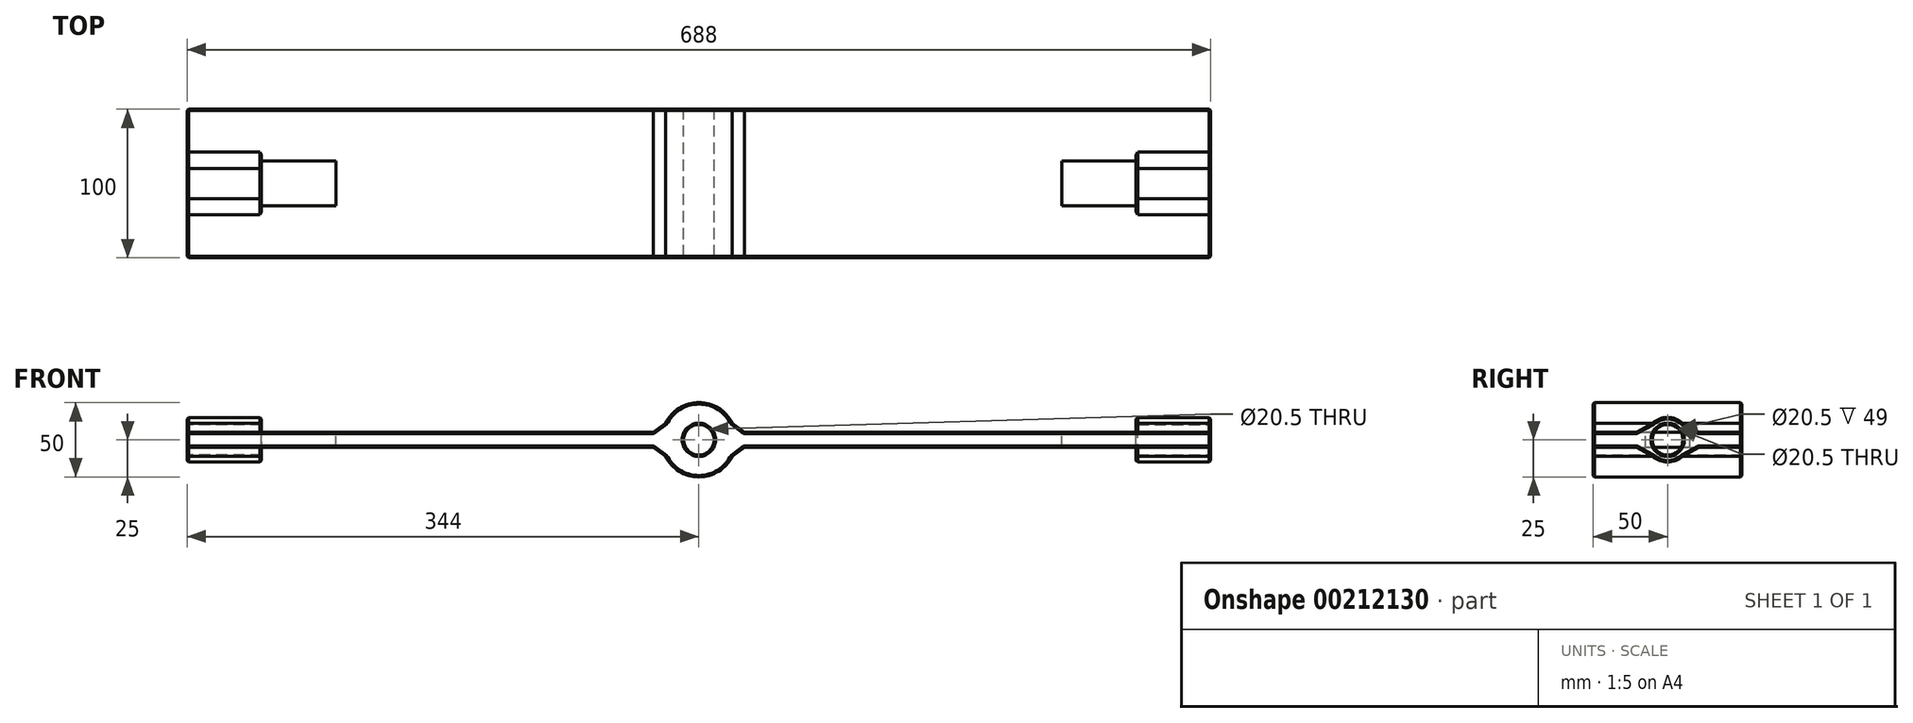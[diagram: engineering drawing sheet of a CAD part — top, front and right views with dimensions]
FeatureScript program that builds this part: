
annotation { "Feature Type Name" : "Feature", "Feature Type Description" : "" }
export const myFeature = defineFeature(function(context is Context, id is Id, definition is map)
    precondition{}
    {
        {
            var Q0;
            Q0=qCreatedBy(makeId("Top.planeOp"),FACE);
            var sketch = newSketch(context, id + "F0", { "sketchPlane" : qUnion([Q0])});
            skLineSegment(sketch, "E0.bottom", {"start": v(344.43, -50.2) * mm, "end": v(-339.43, -50.2) * mm});
            skLineSegment(sketch, "E0.top", {"start": v(344.43, 50.2) * mm, "end": v(-339.43, 50.2) * mm});
            skLineSegment(sketch, "E0.left", {"start": v(344.43, -50.2) * mm, "end": v(344.43, 50.2) * mm});
            skPoint(sketch, "E0.middle", {"position": v(0, 0) * mm});
            skLineSegment(sketch, "E1", {"start": v(-344.43, 14.8) * mm, "end": v(-244.43, 14.8) * mm});
            skLineSegment(sketch, "E2", {"start": v(-244.43, 14.8) * mm, "end": v(-244.43, -15.2) * mm});
            skLineSegment(sketch, "E3", {"start": v(-244.43, -15.2) * mm, "end": v(-344.43, -15.2) * mm});
            skLineSegment(sketch, "E4", {"start": v(-344.43, 45.2) * mm, "end": v(-344.43, 14.8) * mm});
            skLineSegment(sketch, "E5", {"start": v(-344.43, -15.2) * mm, "end": v(-344.43, -45.2) * mm});
            skPoint(sketch, "E6.visualSharp", {"position": v(-344.43, 50.2) * mm});
            skArc(sketch, "E6.filletArc", {"start": v(-339.43, 50.2) * mm, "mid": v(-342.97, 48.73) * mm, "end": v(-344.43, 45.2) * mm});
            skPoint(sketch, "E7.visualSharp", {"position": v(-344.43, -50.2) * mm});
            skArc(sketch, "E7.filletArc", {"start": v(-344.43, -45.2) * mm, "mid": v(-342.97, -48.73) * mm, "end": v(-339.43, -50.2) * mm});
            skLineSegment(sketch, "E8.MirrorCS", {"start": v(244.43, 14.8) * mm, "end": v(244.43, -15.2) * mm});
            skLineSegment(sketch, "E9.MirrorCS", {"start": v(344.43, 14.8) * mm, "end": v(244.43, 14.8) * mm});
            skLineSegment(sketch, "E10.MirrorCS", {"start": v(244.43, -15.2) * mm, "end": v(344.43, -15.2) * mm});
            skLineSegment(sketch, "E11.MirrorCS", {"start": v(344.43, -15.2) * mm, "end": v(344.43, -45.2) * mm});
            skArc(sketch, "E12.MirrorCS", {"start": v(344.43, -45.2) * mm, "mid": v(342.97, -48.73) * mm, "end": v(339.43, -50.2) * mm});
            skArc(sketch, "E13.MirrorCS", {"start": v(339.43, 50.2) * mm, "mid": v(342.97, 48.73) * mm, "end": v(344.43, 45.2) * mm});
            skLineSegment(sketch, "E14", {"start": v(0, 0) * mm, "end": v(0, 50.2) * mm, "construction": true});
            skLineSegment(sketch, "E15", {"start": v(0, 0) * mm, "end": v(0, -50.2) * mm, "construction": true});
            skLineSegment(sketch, "E16.0", {"start": v(27.5, 0) * mm, "end": v(27.5, 50.2) * mm});
            skLineSegment(sketch, "E17.0", {"start": v(-27.5, 0) * mm, "end": v(-27.5, -50.2) * mm});
            skLineSegment(sketch, "E18.0", {"start": v(27.5, 0) * mm, "end": v(27.5, -50.2) * mm});
            skLineSegment(sketch, "E19.0", {"start": v(-27.5, 0) * mm, "end": v(-27.5, 50.2) * mm});
            skSolve(sketch);
        }
        {
            var Q0;
            Q0=qCreatedBy(makeId("Front.planeOp"),FACE);
            var sketch = newSketch(context, id + "F1", { "sketchPlane" : qUnion([Q0])});
            skArc(sketch, "E20", {"start": v(-22.45, -11) * mm, "mid": v(0, -25) * mm, "end": v(22.45, -11) * mm});
            skCircle(sketch, "E21", {"center": v(0, 0) * mm, "radius": 10.25 * mm});
            skLineSegment(sketch, "E22", {"start": v(0, -11) * mm, "end": v(35.57, -11) * mm, "construction": true});
            skLineSegment(sketch, "E23.MirrorCS", {"start": v(0, -11) * mm, "end": v(-35.57, -11) * mm, "construction": true});
            skLineSegment(sketch, "E24.MirrorCS", {"start": v(0, 11) * mm, "end": v(35.57, 11) * mm, "construction": true});
            skLineSegment(sketch, "E25.MirrorCS", {"start": v(0, 11) * mm, "end": v(-35.57, 11) * mm, "construction": true});
            skLineSegment(sketch, "E26", {"start": v(-25, 0) * mm, "end": v(25, 0) * mm, "construction": true});
            skLineSegment(sketch, "E27.0", {"start": v(-24.5, -5) * mm, "end": v(24.5, -5) * mm, "construction": true});
            skLineSegment(sketch, "E28.0", {"start": v(-24.5, 5) * mm, "end": v(24.5, 5) * mm, "construction": true});
            skLineSegment(sketch, "E29", {"start": v(30.5, -14.84) * mm, "end": v(30.5, 11) * mm, "construction": true});
            skLineSegment(sketch, "E30", {"start": v(22.45, 11) * mm, "end": v(30.5, 5) * mm});
            skLineSegment(sketch, "E31", {"start": v(30.5, -5) * mm, "end": v(22.45, -11) * mm});
            skLineSegment(sketch, "E32", {"start": v(-24.5, -5) * mm, "end": v(-24.5, -5) * mm});
            skLineSegment(sketch, "E33", {"start": v(-24.5, 5) * mm, "end": v(-24.5, 5) * mm});
            skLineSegment(sketch, "E34", {"start": v(30.5, 5) * mm, "end": v(344, 5) * mm});
            skLineSegment(sketch, "E35", {"start": v(30.5, -5) * mm, "end": v(344, -5) * mm});
            skLineSegment(sketch, "E36", {"start": v(344, -5) * mm, "end": v(344, 5) * mm});
            skLineSegment(sketch, "E37", {"start": v(-30.5, 5) * mm, "end": v(-344, 5) * mm});
            skLineSegment(sketch, "E38", {"start": v(-30.5, -5) * mm, "end": v(-344, -5) * mm});
            skLineSegment(sketch, "E39", {"start": v(-344, 5) * mm, "end": v(-344, -5) * mm});
            skLineSegment(sketch, "E40", {"start": v(-30.5, 11) * mm, "end": v(-30.5, -11) * mm, "construction": true});
            skLineSegment(sketch, "E41", {"start": v(-22.45, 11) * mm, "end": v(-30.5, 5) * mm});
            skLineSegment(sketch, "E42", {"start": v(-30.5, -5) * mm, "end": v(-22.45, -11) * mm});
            skArc(sketch, "E43.trimOffspring", {"start": v(22.45, 11) * mm, "mid": v(0, 25) * mm, "end": v(-22.45, 11) * mm});
            skLineSegment(sketch, "E44.trimOffspring", {"start": v(30.5, -5) * mm, "end": v(33.37, -5) * mm, "construction": true});
            skSolve(sketch);
        }
        {
            var Q0;
            Q0=makeQuery(id+"F1.imprint","IMPRINT",FACE,{"disambiguationData":[TD([[makeQuery(id+"F1.imprint","IMPRINT",EDGE,{"derivedFrom":sQuery(id+"F1.wireOp",EDGE,"E20")}),1.0]])]});
            extrude(context, id + "F2", {"entities" : qUnion([Q0]), "depth" : 50 * mm, "hasSecondDirection" : true, "secondDirectionOppositeDirection" : true, "secondDirectionDepth" : 50 * mm});
        }
        {
            var Q0;
            Q0=qCreatedBy(makeId("Right.planeOp"),FACE);
            var sketch = newSketch(context, id + "F3", { "sketchPlane" : qUnion([Q0])});
            skCircle(sketch, "E45", {"center": v(0, 0) * mm, "radius": 10.25 * mm});
            skCircle(sketch, "E46", {"center": v(0, 0) * mm, "radius": 15 * mm});
            skSolve(sketch);
        }
        {
            var Q0;
            Q0=makeQuery(id+"F2.opExtrude","SWEPT_FACE",FACE,{"disambiguationData":[OSD([sQuery(id+"F1.wireOp",EDGE,"E39")])]});
            cPlane(context, id + "F4", {"entities" : qUnion([Q0]), "cplaneType" : CPlaneType.OFFSET, "offset" : 50 * mm, "oppositeDirection" : true, "width" : 150 * mm, "height" : 150 * mm});
        }
        {
            var Q0;
            Q0=makeQuery(id+"F2.opExtrude","SWEPT_FACE",FACE,{"disambiguationData":[OSD([sQuery(id+"F1.wireOp",EDGE,"E39")])]});
            var sketch = newSketch(context, id + "F5", { "sketchPlane" : qUnion([Q0])});
            skLineSegment(sketch, "E47.bottom", {"start": v(-15, 5) * mm, "end": v(-14.14, 5) * mm});
            skLineSegment(sketch, "E47.top", {"start": v(-15, -5) * mm, "end": v(-14.14, -5) * mm});
            skLineSegment(sketch, "E47.left", {"start": v(-15, 5) * mm, "end": v(-15, -5) * mm});
            skLineSegment(sketch, "E47.right", {"start": v(15, 5) * mm, "end": v(15, -5) * mm});
            skPoint(sketch, "E47.middle", {"position": v(0, 0) * mm});
            skArc(sketch, "E48", {"start": v(-14.14, 5) * mm, "mid": v(-15, 0) * mm, "end": v(-14.14, -5) * mm});
            skCircle(sketch, "E49", {"center": v(0, 0) * mm, "radius": 10.25 * mm});
            skLineSegment(sketch, "E50.trimOffspring", {"start": v(14.14, -5) * mm, "end": v(15, -5) * mm});
            skLineSegment(sketch, "E51.trimOffspring", {"start": v(14.14, 5) * mm, "end": v(15, 5) * mm});
            skLineSegment(sketch, "E52.trimOffspring", {"start": v(-8.95, -5) * mm, "end": v(8.95, -5) * mm});
            skLineSegment(sketch, "E53.trimOffspring", {"start": v(-8.95, 5) * mm, "end": v(8.95, 5) * mm});
            skLineSegment(sketch, "E54.0", {"start": v(-21, -11) * mm, "end": v(21, -11) * mm, "construction": true});
            skLineSegment(sketch, "E55.0", {"start": v(-21, 11) * mm, "end": v(21, 11) * mm, "construction": true});
            skLineSegment(sketch, "E56.0", {"start": v(21, 13.22) * mm, "end": v(21, -13.2) * mm, "construction": true});
            skLineSegment(sketch, "E57.0", {"start": v(-21, 13.49) * mm, "end": v(-21, -13.28) * mm, "construction": true});
            skLineSegment(sketch, "E58", {"start": v(14.14, -5) * mm, "end": v(21, -5) * mm});
            skLineSegment(sketch, "E59", {"start": v(21, -5) * mm, "end": v(10.2, -11) * mm});
            skLineSegment(sketch, "E60", {"start": v(14.14, 5) * mm, "end": v(21, 5) * mm});
            skLineSegment(sketch, "E61", {"start": v(21, 5) * mm, "end": v(10.2, 11) * mm});
            skLineSegment(sketch, "E62", {"start": v(-10.2, -11) * mm, "end": v(-21, -4.93) * mm});
            skLineSegment(sketch, "E63", {"start": v(-21, -4.93) * mm, "end": v(-14.14, -5) * mm});
            skLineSegment(sketch, "E64", {"start": v(-14.14, 5) * mm, "end": v(-21, 5) * mm});
            skLineSegment(sketch, "E65", {"start": v(-21, 5) * mm, "end": v(-10.2, 11) * mm});
            skArc(sketch, "E66.trimOffspring", {"start": v(-10.2, -11) * mm, "mid": v(0, -15) * mm, "end": v(10.2, -11) * mm});
            skArc(sketch, "E67.trimOffspring", {"start": v(14.14, -5) * mm, "mid": v(15, 0) * mm, "end": v(14.14, 5) * mm});
            skArc(sketch, "E68.trimOffspring", {"start": v(10.2, 11) * mm, "mid": v(0, 15) * mm, "end": v(-10.2, 11) * mm});
            skSolve(sketch);
        }
        {
            var Q0;
            {var subQ0=sQuery(id+"F5.wireOp",EDGE,"E68.trimOffspring");Q0=makeQuery(id+"F5.imprint","IMPRINT",FACE,{"disambiguationData":[TD([[makeQuery(id+"F5.imprint","IMPRINT",EDGE,{"derivedFrom":subQ0}),1.0]])]});}
            var Q1;
            {var subQ10=sQuery(id+"F5.wireOp",EDGE,"E47.top");Q1=makeQuery(id+"F5.imprint","IMPRINT",FACE,{"disambiguationData":[TD([[makeQuery(id+"F5.imprint","IMPRINT",EDGE,{"derivedFrom":subQ10}),-1.0]])]});}
            var Q2;
            {var subQ4=sQuery(id+"F5.wireOp",EDGE,"E47.top");Q2=makeQuery(id+"F5.imprint","IMPRINT",FACE,{"disambiguationData":[TD([[makeQuery(id+"F5.imprint","IMPRINT",EDGE,{"derivedFrom":subQ4}),1.0]])]});}
            extrude(context, id + "F6", {"entities" : qUnion([Q0, Q1, Q2]), "operationType" : NewBodyOperationType.ADD, "oppositeDirection" : true, "depth" : 50 * mm});
        }
        {
            var Q0;
            Q0=qCreatedBy(id+"F4.planeOp",FACE);
            var sketch = newSketch(context, id + "F7", { "sketchPlane" : qUnion([Q0])});
            skLineSegment(sketch, "E69.bottom", {"start": v(-15, -5) * mm, "end": v(15, -5) * mm});
            skLineSegment(sketch, "E69.top", {"start": v(-15, 5) * mm, "end": v(15, 5) * mm});
            skLineSegment(sketch, "E69.left", {"start": v(-15, -5) * mm, "end": v(-15, 5) * mm});
            skLineSegment(sketch, "E69.right", {"start": v(15, -5) * mm, "end": v(15, 5) * mm});
            skPoint(sketch, "E69.middle", {"position": v(0, 0) * mm});
            skSolve(sketch);
        }
        {
            var Q0;
            Q0=makeQuery(id+"F7.imprint","IMPRINT",FACE,{"disambiguationData":[TD([[makeQuery(id+"F7.imprint","IMPRINT",EDGE,{"derivedFrom":sQuery(id+"F7.wireOp",EDGE,"E69.bottom")}),1.0]])]});
            extrude(context, id + "F8", {"entities" : qUnion([Q0]), "operationType" : NewBodyOperationType.REMOVE, "oppositeDirection" : true, "depth" : 50 * mm});
        }
        {
            var Q0;
            Q0=makeQuery(id+"F2.opExtrude","SWEPT_FACE",FACE,{"disambiguationData":[OSD([sQuery(id+"F1.wireOp",EDGE,"E36")])]});
            var sketch = newSketch(context, id + "F9", { "sketchPlane" : qUnion([Q0])});
            skLineSegment(sketch, "E70.bottom", {"start": v(-15, 5) * mm, "end": v(-14.14, 5) * mm});
            skLineSegment(sketch, "E70.top", {"start": v(-15, -5) * mm, "end": v(-14.14, -5) * mm});
            skLineSegment(sketch, "E70.left", {"start": v(-15, 5) * mm, "end": v(-15, -5) * mm});
            skLineSegment(sketch, "E70.right", {"start": v(15, 5) * mm, "end": v(15, -5) * mm});
            skPoint(sketch, "E70.middle", {"position": v(0, 0) * mm});
            skArc(sketch, "E71", {"start": v(-14.14, 5) * mm, "mid": v(-15, 0) * mm, "end": v(-14.14, -5) * mm});
            skCircle(sketch, "E72", {"center": v(0, 0) * mm, "radius": 10.25 * mm});
            skLineSegment(sketch, "E73.trimOffspring", {"start": v(14.14, -5) * mm, "end": v(15, -5) * mm});
            skLineSegment(sketch, "E74.trimOffspring", {"start": v(14.14, 5) * mm, "end": v(15, 5) * mm});
            skLineSegment(sketch, "E75.trimOffspring", {"start": v(-8.95, -5) * mm, "end": v(8.95, -5) * mm});
            skLineSegment(sketch, "E76.trimOffspring", {"start": v(-8.95, 5) * mm, "end": v(8.95, 5) * mm});
            skLineSegment(sketch, "E77.0", {"start": v(-21, -11) * mm, "end": v(21, -11) * mm, "construction": true});
            skLineSegment(sketch, "E78.0", {"start": v(-21, 11) * mm, "end": v(21, 11) * mm, "construction": true});
            skLineSegment(sketch, "E79.0", {"start": v(21, 13.22) * mm, "end": v(21, -13.2) * mm, "construction": true});
            skLineSegment(sketch, "E80.0", {"start": v(-21, 13.49) * mm, "end": v(-21, -13.28) * mm, "construction": true});
            skLineSegment(sketch, "E81", {"start": v(14.14, -5) * mm, "end": v(21, -5) * mm});
            skLineSegment(sketch, "E82", {"start": v(21, -5) * mm, "end": v(10.2, -11) * mm});
            skLineSegment(sketch, "E83", {"start": v(14.14, 5) * mm, "end": v(21, 5) * mm});
            skLineSegment(sketch, "E84", {"start": v(21, 5) * mm, "end": v(10.2, 11) * mm});
            skLineSegment(sketch, "E85", {"start": v(-10.2, -11) * mm, "end": v(-21, -4.93) * mm});
            skLineSegment(sketch, "E86", {"start": v(-21, -4.93) * mm, "end": v(-14.14, -5) * mm});
            skLineSegment(sketch, "E87", {"start": v(-14.14, 5) * mm, "end": v(-21, 5) * mm});
            skLineSegment(sketch, "E88", {"start": v(-21, 5) * mm, "end": v(-10.2, 11) * mm});
            skArc(sketch, "E89.trimOffspring", {"start": v(-10.2, -11) * mm, "mid": v(0, -15) * mm, "end": v(10.2, -11) * mm});
            skArc(sketch, "E90.trimOffspring", {"start": v(14.14, -5) * mm, "mid": v(15, 0) * mm, "end": v(14.14, 5) * mm});
            skArc(sketch, "E91.trimOffspring", {"start": v(10.2, 11) * mm, "mid": v(0, 15) * mm, "end": v(-10.2, 11) * mm});
            skSolve(sketch);
        }
        {
            var Q0;
            Q0=makeQuery(id+"F2.opExtrude","SWEPT_FACE",FACE,{"disambiguationData":[OSD([sQuery(id+"F1.wireOp",EDGE,"E36")])]});
            cPlane(context, id + "F10", {"entities" : qUnion([Q0]), "cplaneType" : CPlaneType.OFFSET, "offset" : 50 * mm, "oppositeDirection" : true, "width" : 150 * mm, "height" : 150 * mm});
        }
        {
            var Q0;
            Q0=makeQuery(id+"F9.imprint","IMPRINT",FACE,{"disambiguationData":[TD([[makeQuery(id+"F9.imprint","IMPRINT",EDGE,{"derivedFrom":sQuery(id+"F9.wireOp",EDGE,"E70.bottom")}),-1.0]])]});
            var Q1;
            {var subQ0=sQuery(id+"F9.wireOp",EDGE,"E71");var subQ4=makeQuery(id+"F9.imprint","INTERSECT",VERTEX,{"derivedFrom":[subQ0,sQuery(id+"F9.wireOp",EDGE,"E74.trimOffspring")]});Q1=makeQuery(id+"F9.imprint","IMPRINT",FACE,{"disambiguationData":[TD([[makeQuery(id+"F9.imprint","IMPRINT",EDGE,{"disambiguationData":[TD([[subQ4,1.0]])],"derivedFrom":subQ0}),1.0]])]});}
            extrude(context, id + "F11", {"entities" : qUnion([Q0, Q1]), "operationType" : NewBodyOperationType.ADD, "oppositeDirection" : true, "depth" : 50 * mm});
        }
        {
            var Q0;
            {var subQ0=sQuery(id+"F9.wireOp",EDGE,"E75.trimOffspring");Q0=makeQuery(id+"F9.imprint","IMPRINT",FACE,{"disambiguationData":[TD([[makeQuery(id+"F9.imprint","IMPRINT",EDGE,{"derivedFrom":subQ0}),1.0]])]});}
            extrude(context, id + "F12", {"entities" : qUnion([Q0]), "operationType" : NewBodyOperationType.REMOVE, "oppositeDirection" : true, "depth" : 50 * mm});
        }
        {
            var Q0;
            Q0=qCreatedBy(id+"F10.planeOp",FACE);
            var sketch = newSketch(context, id + "F17", { "sketchPlane" : qUnion([Q0])});
            skLineSegment(sketch, "E92.bottom", {"start": v(-15, -5) * mm, "end": v(15, -5) * mm});
            skLineSegment(sketch, "E92.top", {"start": v(-15, 5) * mm, "end": v(15, 5) * mm});
            skLineSegment(sketch, "E92.left", {"start": v(-15, -5) * mm, "end": v(-15, 5) * mm});
            skLineSegment(sketch, "E92.right", {"start": v(15, -5) * mm, "end": v(15, 5) * mm});
            skPoint(sketch, "E92.middle", {"position": v(0, 0) * mm});
            skSolve(sketch);
        }
        {
            var Q0;
            Q0=makeQuery(id+"F17.imprint","IMPRINT",FACE,{"disambiguationData":[TD([[makeQuery(id+"F17.imprint","IMPRINT",EDGE,{"derivedFrom":sQuery(id+"F17.wireOp",EDGE,"E92.bottom")}),1.0]])]});
            extrude(context, id + "F13", {"entities" : qUnion([Q0]), "operationType" : NewBodyOperationType.REMOVE, "oppositeDirection" : true, "depth" : 50 * mm});
        }
        {
            var Q0;
            {var subQ0=sQuery(id+"F5.wireOp",EDGE,"E52.trimOffspring");Q0=makeQuery(id+"F5.imprint","IMPRINT",FACE,{"disambiguationData":[TD([[makeQuery(id+"F5.imprint","IMPRINT",EDGE,{"derivedFrom":subQ0}),-1.0]])]});}
            extrude(context, id + "F14", {"entities" : qUnion([Q0]), "operationType" : NewBodyOperationType.REMOVE, "oppositeDirection" : true, "depth" : 50 * mm});
        }
        {
            var Q0;
            {var subQ10=sQuery(id+"F9.wireOp",EDGE,"E70.top");Q0=makeQuery(id+"F9.imprint","IMPRINT",FACE,{"disambiguationData":[TD([[makeQuery(id+"F9.imprint","IMPRINT",EDGE,{"derivedFrom":subQ10}),-1.0]])]});}
            var Q1;
            {var subQ0=sQuery(id+"F9.wireOp",EDGE,"E84");Q1=makeQuery(id+"F9.imprint","IMPRINT",FACE,{"disambiguationData":[TD([[makeQuery(id+"F9.imprint","IMPRINT",EDGE,{"derivedFrom":subQ0}),1.0]])]});}
            extrude(context, id + "F15", {"entities" : qUnion([Q0, Q1]), "operationType" : NewBodyOperationType.ADD, "oppositeDirection" : true, "depth" : 50 * mm});
        }
        {
            var Q0;
            Q0=makeQuery(id+"F2.opExtrude","CAP_FACE",FACE,{"disambiguationData":[OSD([sQuery(id+"F1.wireOp",EDGE,"E20"),sQuery(id+"F1.wireOp",EDGE,"E21"),sQuery(id+"F1.wireOp",EDGE,"E30"),sQuery(id+"F1.wireOp",EDGE,"E31"),sQuery(id+"F1.wireOp",EDGE,"E34"),sQuery(id+"F1.wireOp",EDGE,"E35"),sQuery(id+"F1.wireOp",EDGE,"E36"),sQuery(id+"F1.wireOp",EDGE,"E37"),sQuery(id+"F1.wireOp",EDGE,"E38"),sQuery(id+"F1.wireOp",EDGE,"E39"),sQuery(id+"F1.wireOp",EDGE,"E41"),sQuery(id+"F1.wireOp",EDGE,"E42"),sQuery(id+"F1.wireOp",EDGE,"E43.trimOffspring")])],"isStart":false});
            var Q1;
            Q1=makeQuery(id+"F2.opExtrude","CAP_FACE",FACE,{"disambiguationData":[OSD([sQuery(id+"F1.wireOp",EDGE,"E20"),sQuery(id+"F1.wireOp",EDGE,"E21"),sQuery(id+"F1.wireOp",EDGE,"E30"),sQuery(id+"F1.wireOp",EDGE,"E31"),sQuery(id+"F1.wireOp",EDGE,"E34"),sQuery(id+"F1.wireOp",EDGE,"E35"),sQuery(id+"F1.wireOp",EDGE,"E36"),sQuery(id+"F1.wireOp",EDGE,"E37"),sQuery(id+"F1.wireOp",EDGE,"E38"),sQuery(id+"F1.wireOp",EDGE,"E39"),sQuery(id+"F1.wireOp",EDGE,"E41"),sQuery(id+"F1.wireOp",EDGE,"E42"),sQuery(id+"F1.wireOp",EDGE,"E43.trimOffspring")])],"isStart":true});
            var Q2;
            {var subQ0=sQuery(id+"F5.wireOp",EDGE,"E49");var subQ1=sQuery(id+"F1.wireOp",EDGE,"E39");Q2=makeQuery(id+"F6.boolean.opBoolean","MERGE",FACE,{"derivedFrom":[makeQuery(id+"F2.opExtrude","SWEPT_FACE",FACE,{"disambiguationData":[OSD([subQ1])]}),makeQuery(id+"F6.opExtrude","CAP_FACE",FACE,{"disambiguationData":[OSD([sQuery(id+"F1.wireOp",EDGE,"E38"),subQ1,sQuery(id+"F5.wireOp",EDGE,"E47.left"),subQ0,sQuery(id+"F5.wireOp",EDGE,"E58"),sQuery(id+"F5.wireOp",EDGE,"E59"),sQuery(id+"F5.wireOp",EDGE,"E62"),sQuery(id+"F5.wireOp",EDGE,"E63"),sQuery(id+"F5.wireOp",EDGE,"E66.trimOffspring")])],"isStart":true}),makeQuery(id+"F6.opExtrude","CAP_FACE",FACE,{"disambiguationData":[OSD([sQuery(id+"F1.wireOp",EDGE,"E37"),subQ1,subQ0,sQuery(id+"F5.wireOp",EDGE,"E60"),sQuery(id+"F5.wireOp",EDGE,"E61"),sQuery(id+"F5.wireOp",EDGE,"E64"),sQuery(id+"F5.wireOp",EDGE,"E65"),sQuery(id+"F5.wireOp",EDGE,"E68.trimOffspring")])],"isStart":true})]});}
            var Q3;
            {var subQ0=sQuery(id+"F9.wireOp",EDGE,"E72");var subQ1=sQuery(id+"F1.wireOp",EDGE,"E36");var subQ2=sQuery(id+"F1.wireOp",EDGE,"E34");var subQ3=sQuery(id+"F1.wireOp",EDGE,"E35");var subQ16=sQuery(id+"F9.wireOp",EDGE,"E75.trimOffspring");var subQ17=makeQuery(id+"F2.opExtrude","SWEPT_EDGE",EDGE,{"disambiguationData":[OSD([subQ3,subQ1])]});var subQ20=makeQuery(id+"F2.opExtrude","SWEPT_FACE",FACE,{"disambiguationData":[OSD([subQ1])]});Q3=makeQuery(id+"F15.boolean.opBoolean","MERGE",FACE,{"derivedFrom":[makeQuery(id+"F12.boolean.opBoolean","SPLIT",FACE,{"disambiguationData":[TD([makeQuery(id+"F12.opExtrude","SWEPT_FACE",FACE,{"disambiguationData":[OSD([subQ0]),TDD([makeQuery(id+"F9.imprint","IMPRINT",EDGE,{"disambiguationData":[TD([[makeQuery(id+"F9.imprint","INTERSECT",VERTEX,{"disambiguationData":[OD(1.0)],"derivedFrom":[subQ17,subQ0,subQ16]}),-1.0]])],"derivedFrom":subQ0})])]})])],"derivedFrom":subQ20}),makeQuery(id+"F12.boolean.opBoolean","SPLIT",FACE,{"disambiguationData":[TD([makeQuery(id+"F12.opExtrude","SWEPT_FACE",FACE,{"disambiguationData":[OSD([subQ0]),TDD([makeQuery(id+"F9.imprint","IMPRINT",EDGE,{"disambiguationData":[TD([[makeQuery(id+"F9.imprint","INTERSECT",VERTEX,{"disambiguationData":[OD(0.0)],"derivedFrom":[subQ17,subQ0,subQ16]}),1.0]])],"derivedFrom":subQ0})])]})])],"derivedFrom":subQ20}),makeQuery(id+"F15.opExtrude","CAP_FACE",FACE,{"disambiguationData":[OSD([subQ3,subQ1,sQuery(id+"F9.wireOp",EDGE,"E70.top"),subQ0,sQuery(id+"F9.wireOp",EDGE,"E81"),sQuery(id+"F9.wireOp",EDGE,"E82"),sQuery(id+"F9.wireOp",EDGE,"E85"),sQuery(id+"F9.wireOp",EDGE,"E89.trimOffspring")])],"isStart":true}),makeQuery(id+"F15.opExtrude","CAP_FACE",FACE,{"disambiguationData":[OSD([subQ2,subQ1,subQ0,sQuery(id+"F9.wireOp",EDGE,"E83"),sQuery(id+"F9.wireOp",EDGE,"E84"),sQuery(id+"F9.wireOp",EDGE,"E87"),sQuery(id+"F9.wireOp",EDGE,"E88"),sQuery(id+"F9.wireOp",EDGE,"E91.trimOffspring")])],"isStart":true})]});}
            var Q4;
            {var subQ0=sQuery(id+"F9.wireOp",EDGE,"E75.trimOffspring");var subQ1=sQuery(id+"F9.wireOp",EDGE,"E72");var subQ2=sQuery(id+"F1.wireOp",EDGE,"E36");var subQ3=makeQuery(id+"F2.opExtrude","SWEPT_EDGE",EDGE,{"disambiguationData":[OSD([sQuery(id+"F1.wireOp",EDGE,"E35"),subQ2])]});var subQ4=makeQuery(id+"F9.imprint","INTERSECT",VERTEX,{"disambiguationData":[OD(0.0)],"derivedFrom":[subQ3,subQ1,subQ0]});var subQ5=makeQuery(id+"F9.imprint","INTERSECT",VERTEX,{"disambiguationData":[OD(1.0)],"derivedFrom":[subQ3,subQ1,subQ0]});var subQ6=sQuery(id+"F9.wireOp",EDGE,"E76.trimOffspring");var subQ7=makeQuery(id+"F2.opExtrude","SWEPT_EDGE",EDGE,{"disambiguationData":[OSD([sQuery(id+"F1.wireOp",EDGE,"E34"),subQ2])]});var subQ8=makeQuery(id+"F9.imprint","INTERSECT",VERTEX,{"disambiguationData":[OD(0.0)],"derivedFrom":[subQ7,subQ1,subQ6]});Q4=makeQuery(id+"F15.boolean.opBoolean","MERGE",EDGE,{"derivedFrom":[makeQuery(id+"F12.boolean.opBoolean","COPY",EDGE,{"derivedFrom":makeQuery(id+"F12.opExtrude","CAP_EDGE",EDGE,{"disambiguationData":[OSD([subQ1]),TDD([makeQuery(id+"F9.imprint","IMPRINT",EDGE,{"disambiguationData":[TD([[subQ4,1.0]])],"derivedFrom":subQ1})])],"isStart":false})}),makeQuery(id+"F12.boolean.opBoolean","COPY",EDGE,{"derivedFrom":makeQuery(id+"F12.opExtrude","CAP_EDGE",EDGE,{"disambiguationData":[OSD([subQ1]),TDD([makeQuery(id+"F9.imprint","IMPRINT",EDGE,{"disambiguationData":[TD([[subQ5,-1.0]])],"derivedFrom":subQ1})])],"isStart":false})}),makeQuery(id+"F15.opExtrude","CAP_EDGE",EDGE,{"disambiguationData":[OSD([subQ1]),TDD([makeQuery(id+"F9.imprint","IMPRINT",EDGE,{"disambiguationData":[TD([[subQ8,1.0]])],"derivedFrom":subQ1})])],"isStart":false}),makeQuery(id+"F15.opExtrude","CAP_EDGE",EDGE,{"disambiguationData":[OSD([subQ1]),TDD([makeQuery(id+"F9.imprint","IMPRINT",EDGE,{"disambiguationData":[TD([[subQ4,-1.0]])],"derivedFrom":subQ1})])],"isStart":false})]});}
            var Q5;
            Q5=makeQuery(id+"F15.opExtrude","CAP_EDGE",EDGE,{"disambiguationData":[OSD([sQuery(id+"F9.wireOp",EDGE,"E88")])],"isStart":false});
            var Q6;
            Q6=makeQuery(id+"F15.opExtrude","CAP_EDGE",EDGE,{"disambiguationData":[OSD([sQuery(id+"F9.wireOp",EDGE,"E91.trimOffspring")])],"isStart":false});
            var Q7;
            Q7=makeQuery(id+"F15.opExtrude","CAP_EDGE",EDGE,{"disambiguationData":[OSD([sQuery(id+"F9.wireOp",EDGE,"E84")])],"isStart":false});
            var Q8;
            Q8=makeQuery(id+"F15.opExtrude","CAP_EDGE",EDGE,{"disambiguationData":[OSD([sQuery(id+"F9.wireOp",EDGE,"E89.trimOffspring")])],"isStart":false});
            var Q9;
            Q9=makeQuery(id+"F15.opExtrude","CAP_EDGE",EDGE,{"disambiguationData":[OSD([sQuery(id+"F9.wireOp",EDGE,"E85")])],"isStart":false});
            var Q10;
            Q10=makeQuery(id+"F15.opExtrude","CAP_EDGE",EDGE,{"disambiguationData":[OSD([sQuery(id+"F9.wireOp",EDGE,"E82")])],"isStart":false});
            var Q11;
            Q11=makeQuery(id+"F13.boolean.opBoolean","COPY",EDGE,{"derivedFrom":makeQuery(id+"F13.opExtrude","SWEPT_EDGE",EDGE,{"disambiguationData":[OSD([sQuery(id+"F17.wireOp",EDGE,"E92.top"),sQuery(id+"F17.wireOp",EDGE,"E92.left")])]})});
            var Q12;
            Q12=makeQuery(id+"F13.boolean.opBoolean","COPY",EDGE,{"derivedFrom":makeQuery(id+"F13.opExtrude","SWEPT_EDGE",EDGE,{"disambiguationData":[OSD([sQuery(id+"F17.wireOp",EDGE,"E92.bottom"),sQuery(id+"F17.wireOp",EDGE,"E92.left")])]})});
            var Q13;
            Q13=makeQuery(id+"F13.boolean.opBoolean","COPY",EDGE,{"derivedFrom":makeQuery(id+"F13.opExtrude","CAP_EDGE",EDGE,{"disambiguationData":[OSD([sQuery(id+"F17.wireOp",EDGE,"E92.top")])],"isStart":false})});
            var Q14;
            Q14=makeQuery(id+"F13.boolean.opBoolean","COPY",EDGE,{"derivedFrom":makeQuery(id+"F13.opExtrude","CAP_EDGE",EDGE,{"disambiguationData":[OSD([sQuery(id+"F17.wireOp",EDGE,"E92.bottom")])],"isStart":false})});
            var Q15;
            Q15=makeQuery(id+"F13.boolean.opBoolean","COPY",EDGE,{"derivedFrom":makeQuery(id+"F13.opExtrude","SWEPT_EDGE",EDGE,{"disambiguationData":[OSD([sQuery(id+"F17.wireOp",EDGE,"E92.bottom"),sQuery(id+"F17.wireOp",EDGE,"E92.right")])]})});
            var Q16;
            Q16=makeQuery(id+"F13.boolean.opBoolean","COPY",EDGE,{"derivedFrom":makeQuery(id+"F13.opExtrude","SWEPT_EDGE",EDGE,{"disambiguationData":[OSD([sQuery(id+"F17.wireOp",EDGE,"E92.top"),sQuery(id+"F17.wireOp",EDGE,"E92.right")])]})});
            var Q17;
            {var subQ0=sQuery(id+"F5.wireOp",EDGE,"E52.trimOffspring");var subQ1=sQuery(id+"F5.wireOp",EDGE,"E49");var subQ2=sQuery(id+"F1.wireOp",EDGE,"E39");var subQ3=makeQuery(id+"F2.opExtrude","SWEPT_EDGE",EDGE,{"disambiguationData":[OSD([sQuery(id+"F1.wireOp",EDGE,"E38"),subQ2])]});var subQ4=makeQuery(id+"F5.imprint","INTERSECT",VERTEX,{"disambiguationData":[OD(0.0)],"derivedFrom":[subQ3,subQ1,subQ0]});var subQ5=sQuery(id+"F5.wireOp",EDGE,"E53.trimOffspring");var subQ6=makeQuery(id+"F2.opExtrude","SWEPT_EDGE",EDGE,{"disambiguationData":[OSD([sQuery(id+"F1.wireOp",EDGE,"E37"),subQ2])]});var subQ7=makeQuery(id+"F5.imprint","INTERSECT",VERTEX,{"disambiguationData":[OD(0.0)],"derivedFrom":[subQ6,subQ1,subQ5]});var subQ8=makeQuery(id+"F5.imprint","INTERSECT",VERTEX,{"disambiguationData":[OD(1.0)],"derivedFrom":[subQ3,subQ1,subQ0]});Q17=makeQuery(id+"F14.boolean.opBoolean","MERGE",EDGE,{"derivedFrom":[makeQuery(id+"F6.opExtrude","CAP_EDGE",EDGE,{"disambiguationData":[OSD([subQ1]),TDD([makeQuery(id+"F5.imprint","IMPRINT",EDGE,{"disambiguationData":[TD([[subQ7,-1.0]])],"derivedFrom":subQ1})])],"isStart":false}),makeQuery(id+"F6.opExtrude","CAP_EDGE",EDGE,{"disambiguationData":[OSD([subQ1]),TDD([makeQuery(id+"F5.imprint","IMPRINT",EDGE,{"disambiguationData":[TD([[subQ4,1.0]])],"derivedFrom":subQ1})])],"isStart":false}),makeQuery(id+"F14.opExtrude","CAP_EDGE",EDGE,{"disambiguationData":[OSD([subQ1]),TDD([makeQuery(id+"F5.imprint","IMPRINT",EDGE,{"disambiguationData":[TD([[subQ8,1.0]])],"derivedFrom":subQ1})])],"isStart":false}),makeQuery(id+"F14.opExtrude","CAP_EDGE",EDGE,{"disambiguationData":[OSD([subQ1]),TDD([makeQuery(id+"F5.imprint","IMPRINT",EDGE,{"disambiguationData":[TD([[subQ4,-1.0]])],"derivedFrom":subQ1})])],"isStart":false})]});}
            var Q18;
            Q18=makeQuery(id+"F6.opExtrude","CAP_EDGE",EDGE,{"disambiguationData":[OSD([sQuery(id+"F5.wireOp",EDGE,"E65")])],"isStart":false});
            var Q19;
            Q19=makeQuery(id+"F6.opExtrude","CAP_EDGE",EDGE,{"disambiguationData":[OSD([sQuery(id+"F5.wireOp",EDGE,"E68.trimOffspring")])],"isStart":false});
            var Q20;
            Q20=makeQuery(id+"F6.opExtrude","CAP_EDGE",EDGE,{"disambiguationData":[OSD([sQuery(id+"F5.wireOp",EDGE,"E61")])],"isStart":false});
            var Q21;
            Q21=makeQuery(id+"F6.opExtrude","CAP_EDGE",EDGE,{"disambiguationData":[OSD([sQuery(id+"F5.wireOp",EDGE,"E59")])],"isStart":false});
            var Q22;
            Q22=makeQuery(id+"F6.opExtrude","CAP_EDGE",EDGE,{"disambiguationData":[OSD([sQuery(id+"F5.wireOp",EDGE,"E66.trimOffspring")])],"isStart":false});
            var Q23;
            Q23=makeQuery(id+"F6.opExtrude","CAP_EDGE",EDGE,{"disambiguationData":[OSD([sQuery(id+"F5.wireOp",EDGE,"E62")])],"isStart":false});
            var Q24;
            Q24=makeQuery(id+"F8.boolean.opBoolean","COPY",EDGE,{"derivedFrom":makeQuery(id+"F8.opExtrude","SWEPT_EDGE",EDGE,{"disambiguationData":[OSD([sQuery(id+"F7.wireOp",EDGE,"E69.bottom"),sQuery(id+"F7.wireOp",EDGE,"E69.right")])]})});
            var Q25;
            Q25=makeQuery(id+"F8.boolean.opBoolean","COPY",EDGE,{"derivedFrom":makeQuery(id+"F8.opExtrude","SWEPT_EDGE",EDGE,{"disambiguationData":[OSD([sQuery(id+"F7.wireOp",EDGE,"E69.top"),sQuery(id+"F7.wireOp",EDGE,"E69.right")])]})});
            var Q26;
            Q26=makeQuery(id+"F8.boolean.opBoolean","COPY",EDGE,{"derivedFrom":makeQuery(id+"F8.opExtrude","CAP_EDGE",EDGE,{"disambiguationData":[OSD([sQuery(id+"F7.wireOp",EDGE,"E69.bottom")])],"isStart":false})});
            var Q27;
            Q27=makeQuery(id+"F8.boolean.opBoolean","COPY",EDGE,{"derivedFrom":makeQuery(id+"F8.opExtrude","CAP_EDGE",EDGE,{"disambiguationData":[OSD([sQuery(id+"F7.wireOp",EDGE,"E69.top")])],"isStart":false})});
            var Q28;
            Q28=makeQuery(id+"F8.boolean.opBoolean","COPY",EDGE,{"derivedFrom":makeQuery(id+"F8.opExtrude","SWEPT_EDGE",EDGE,{"disambiguationData":[OSD([sQuery(id+"F7.wireOp",EDGE,"E69.top"),sQuery(id+"F7.wireOp",EDGE,"E69.left")])]})});
            var Q29;
            Q29=makeQuery(id+"F8.boolean.opBoolean","COPY",EDGE,{"derivedFrom":makeQuery(id+"F8.opExtrude","SWEPT_EDGE",EDGE,{"disambiguationData":[OSD([sQuery(id+"F7.wireOp",EDGE,"E69.bottom"),sQuery(id+"F7.wireOp",EDGE,"E69.left")])]})});
            chamfer(context, id + "F16", {"entities" : qUnion([Q0, Q1, Q2, Q3, Q4, Q5, Q6, Q7, Q8, Q9, Q10, Q11, Q12, Q13, Q14, Q15, Q16, Q17, Q18, Q19, Q20, Q21, Q22, Q23, Q24, Q25, Q26, Q27, Q28, Q29]), "width" : 1 * mm, "tangentPropagation" : true});
        }
    });
